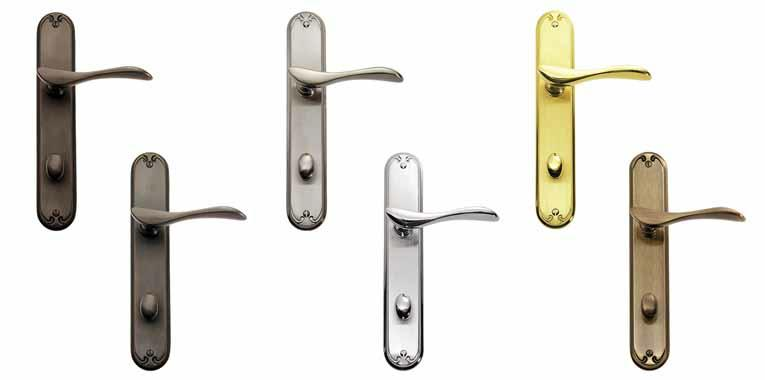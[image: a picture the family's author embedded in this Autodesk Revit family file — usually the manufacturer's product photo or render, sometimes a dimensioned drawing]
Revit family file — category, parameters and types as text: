
# Revit family: Door-French-Pella-Architect_Series-Hinged_Patio_Door-InSwing-Right_Left
name_source: partatom
category: Doors
revit_build: Autodesk Revit Architecture 2013 (Build: 20130531_2115(x64)
units: mm (PartAtom-declared; Revit-internal decimal feet)

## types (30) — shared parameters
Analytic Construction = <None>
Architectural Design Manual = www.pellaadm.com
Construction Type = -
Cross Grille Pattern = No
Custom Grille Pattern = No
Custom Horizontal Lites = 2
Custom Vertical Lites = 6
Description = In-Swing - Right Left Hand Operation
Door Grille Visibility = Yes
Door Handle Height = 3' - 0"
Energy Efficiency = http://www.pella.com
Environmental Commitment = http://www.pella.com
Ext Finish = Aluminum - Pella - Brown
Function = Interior
Glazing Finish = Glass - Pella - Clear Insulating Glass
Glazing Thickness = 107/128"
Int Finish = Wood - Pella - Pine
Manufacturer = Pella - Windows & Doors
Note* = Maximum Frame Depth is 211 mm; if Wall Depth exceeds this value please recalculated Set Back to reflect
Operation = Hinged Patio Door
Prairie Grille Pattern = No
Product Documentation Link = http://media.pella.com
Product Name = Architect Series Hinged Patio Door
Product Page URL = http://www.pella.com
Series = Architect Series - Aluminum-Clad Wood
Thickness = 0"
Top Row Grille Pattern = No
Traditional Grille Pattern = Yes
URL = www.pella.com
Wall Closure = By host

## per-type parameters (varying)
| type | C Height | C Width | DLO Height | DLO Width | Height | Hinges | Rough Height | Rough Width | Unit Height | Unit Width | Width |
| 2680 | 6' - 8 1/8" | 2' - 1 3/8" | 5' - 4 9/256" | 1' - 1 41/128" | 6' - 7 1/2" | 3 | 6' - 8 5/8" | 2' - 2 1/8" | 6' - 5 1/4" | 1' - 11 15/128" | 2' - 1 3/8" |
| 2681 | 6' - 8 1/8" | 2' - 1 3/8" | 5' - 4 9/256" | 1' - 1 41/128" | 6' - 8 1/8" | 3 | 6' - 8 5/8" | 2' - 2 1/8" | 6' - 5 1/4" | 1' - 11 15/128" | 2' - 1 3/8" |
| 2682 | 6' - 9 1/2" | 2' - 1 3/8" | 5' - 5 105/256" | 1' - 1 41/128" | 6' - 9 1/2" | 3 | 6' - 10" | 2' - 2 1/8" | 6' - 6 5/8" | 1' - 11 15/128" | 2' - 1 3/8" |
| 2686 | 7' - 2" | 2' - 1 3/8" | 5' - 9 233/256" | 1' - 1 41/128" | 7' - 2" | 4 | 7' - 2 1/2" | 2' - 2 1/8" | 6' - 11 1/8" | 1' - 11 15/128" | 2' - 1 3/8" |
| 2696 | 7' - 11 1/2" | 2' - 1 3/8" | 6' - 7 105/256" | 1' - 1 41/128" | 7' - 11 1/2" | 4 | 8' - 0" | 2' - 2 1/8" | 7' - 8 5/8" | 1' - 11 15/128" | 2' - 1 3/8" |
| 26120 | 9' - 11 1/2" | 2' - 1 3/8" | 8' - 7 105/256" | 1' - 1 41/128" | 9' - 11 1/2" | 4 | 10' - 0" | 2' - 2 1/8" | 9' - 8 5/8" | 1' - 11 15/128" | 2' - 1 3/8" |
| 3080 | 6' - 8 1/8" | 2' - 6" | 5' - 4 9/256" | 1' - 5 121/128" | 6' - 7 1/2" | 3 | 6' - 8 5/8" | 2' - 6 3/4" | 6' - 5 1/4" | 2' - 3 95/128" | 2' - 6" |
| 3081 | 6' - 8 1/8" | 2' - 6" | 5' - 4 9/256" | 1' - 5 121/128" | 6' - 8 1/8" | 3 | 6' - 8 5/8" | 2' - 6 3/4" | 6' - 5 1/4" | 2' - 3 95/128" | 2' - 6" |
| 3082 | 6' - 9 1/2" | 2' - 6" | 5' - 5 105/256" | 1' - 5 121/128" | 6' - 9 1/2" | 3 | 6' - 10" | 2' - 6 3/4" | 6' - 6 5/8" | 2' - 3 95/128" | 2' - 6" |
| 3086 | 7' - 2" | 2' - 6" | 5' - 9 233/256" | 1' - 5 121/128" | 7' - 2" | 4 | 7' - 2 1/2" | 2' - 6 3/4" | 6' - 11 1/8" | 2' - 3 95/128" | 2' - 6" |
| 3096 | 7' - 11 1/2" | 2' - 6" | 6' - 7 105/256" | 1' - 5 121/128" | 7' - 11 1/2" | 4 | 8' - 0" | 2' - 6 3/4" | 7' - 8 5/8" | 2' - 3 95/128" | 2' - 6" |
| 30120 | 9' - 11 1/2" | 2' - 6" | 8' - 7 105/256" | 1' - 5 121/128" | 9' - 11 1/2" | 4 | 10' - 0" | 2' - 6 3/4" | 9' - 8 5/8" | 2' - 3 95/128" | 2' - 6" |
| 3480 | 6' - 8 1/8" | 2' - 9 1/2" | 5' - 4 9/256" | 1' - 9 57/128" | 6' - 7 1/2" | 3 | 6' - 8 5/8" | 2' - 10 1/4" | 6' - 5 1/4" | 2' - 7 31/128" | 2' - 9 1/2" |
| 3481 | 6' - 8 1/8" | 2' - 9 1/2" | 5' - 4 9/256" | 1' - 9 57/128" | 6' - 8 1/8" | 3 | 6' - 8 5/8" | 2' - 10 1/4" | 6' - 5 1/4" | 2' - 7 31/128" | 2' - 9 1/2" |
| 3482 | 6' - 9 1/2" | 2' - 9 1/2" | 5' - 5 105/256" | 1' - 9 57/128" | 6' - 9 1/2" | 3 | 6' - 10" | 2' - 10 1/4" | 6' - 6 5/8" | 2' - 7 31/128" | 2' - 9 1/2" |
| 3486 | 7' - 2" | 2' - 9 1/2" | 5' - 9 233/256" | 1' - 9 57/128" | 7' - 2" | 4 | 7' - 2 1/2" | 2' - 10 1/4" | 6' - 11 1/8" | 2' - 7 31/128" | 2' - 9 1/2" |
| 3496 | 7' - 11 1/2" | 2' - 9 1/2" | 6' - 7 105/256" | 1' - 9 57/128" | 7' - 11 1/2" | 4 | 8' - 0" | 2' - 10 1/4" | 7' - 8 5/8" | 2' - 7 31/128" | 2' - 9 1/2" |
| 34120 | 9' - 11 1/2" | 2' - 9 1/2" | 8' - 7 105/256" | 1' - 9 57/128" | 9' - 11 1/2" | 4 | 10' - 0" | 2' - 10 1/4" | 9' - 8 5/8" | 2' - 7 31/128" | 2' - 9 1/2" |
| 3680 | 6' - 8 1/8" | 3' - 0" | 5' - 4 9/256" | 1' - 11 121/128" | 6' - 7 1/2" | 3 | 6' - 8 5/8" | 3' - 0 3/4" | 6' - 5 1/4" | 2' - 9 95/128" | 3' - 0" |
| 3681 | 6' - 8 1/8" | 3' - 0" | 5' - 4 9/256" | 1' - 11 121/128" | 6' - 8 1/8" | 3 | 6' - 8 5/8" | 3' - 0 3/4" | 6' - 5 1/4" | 2' - 9 95/128" | 3' - 0" |
| 3682 | 6' - 9 1/2" | 3' - 0" | 5' - 5 105/256" | 1' - 11 121/128" | 6' - 9 1/2" | 3 | 6' - 10" | 3' - 0 3/4" | 6' - 6 5/8" | 2' - 9 95/128" | 3' - 0" |
| 3686 | 7' - 2" | 3' - 0" | 5' - 9 233/256" | 1' - 11 121/128" | 7' - 2" | 4 | 7' - 2 1/2" | 3' - 0 3/4" | 6' - 11 1/8" | 2' - 9 95/128" | 3' - 0" |
| 3696 | 7' - 11 1/2" | 3' - 0" | 6' - 7 105/256" | 1' - 11 121/128" | 7' - 11 1/2" | 4 | 8' - 0" | 3' - 0 3/4" | 7' - 8 5/8" | 2' - 9 95/128" | 3' - 0" |
| 36120 | 9' - 11 1/2" | 3' - 0" | 8' - 7 105/256" | 1' - 11 121/128" | 9' - 11 1/2" | 4 | 10' - 0" | 3' - 0 3/4" | 9' - 8 5/8" | 2' - 9 95/128" | 3' - 0" |
| 3880 | 6' - 8 1/8" | 3' - 1 7/8" | 5' - 4 9/256" | 2' - 1 105/128" | 6' - 7 1/2" | 3 | 6' - 8 5/8" | 3' - 2 5/8" | 6' - 5 1/4" | 2' - 11 79/128" | 3' - 1 7/8" |
| 3881 | 6' - 8 1/8" | 3' - 1 7/8" | 5' - 4 9/256" | 2' - 1 105/128" | 6' - 8 1/8" | 3 | 6' - 8 5/8" | 3' - 2 5/8" | 6' - 5 1/4" | 2' - 11 79/128" | 3' - 1 7/8" |
| 3882 | 6' - 9 1/2" | 3' - 1 7/8" | 5' - 5 105/256" | 2' - 1 105/128" | 6' - 9 1/2" | 3 | 6' - 10" | 3' - 2 5/8" | 6' - 6 5/8" | 2' - 11 79/128" | 3' - 1 7/8" |
| 3886 | 7' - 2" | 3' - 1 7/8" | 5' - 9 233/256" | 2' - 1 105/128" | 7' - 2" | 4 | 7' - 2 1/2" | 3' - 2 5/8" | 6' - 11 1/8" | 2' - 11 79/128" | 3' - 1 7/8" |
| 3896 | 7' - 11 1/2" | 3' - 1 7/8" | 6' - 7 105/256" | 2' - 1 105/128" | 7' - 11 1/2" | 4 | 8' - 0" | 3' - 2 5/8" | 7' - 8 5/8" | 2' - 11 79/128" | 3' - 1 7/8" |
| 38120 | 9' - 11 1/2" | 3' - 1 7/8" | 8' - 7 105/256" | 2' - 1 105/128" | 9' - 11 1/2" | 4 | 10' - 0" | 3' - 2 5/8" | 9' - 8 5/8" | 2' - 11 79/128" | 3' - 1 7/8" |

note: column(s) folded — value = type name in every type: Model

## geometry (parser evidence)
native form markers: Blend x6, Sweep x8
no freeform markers — native parametric forms only
